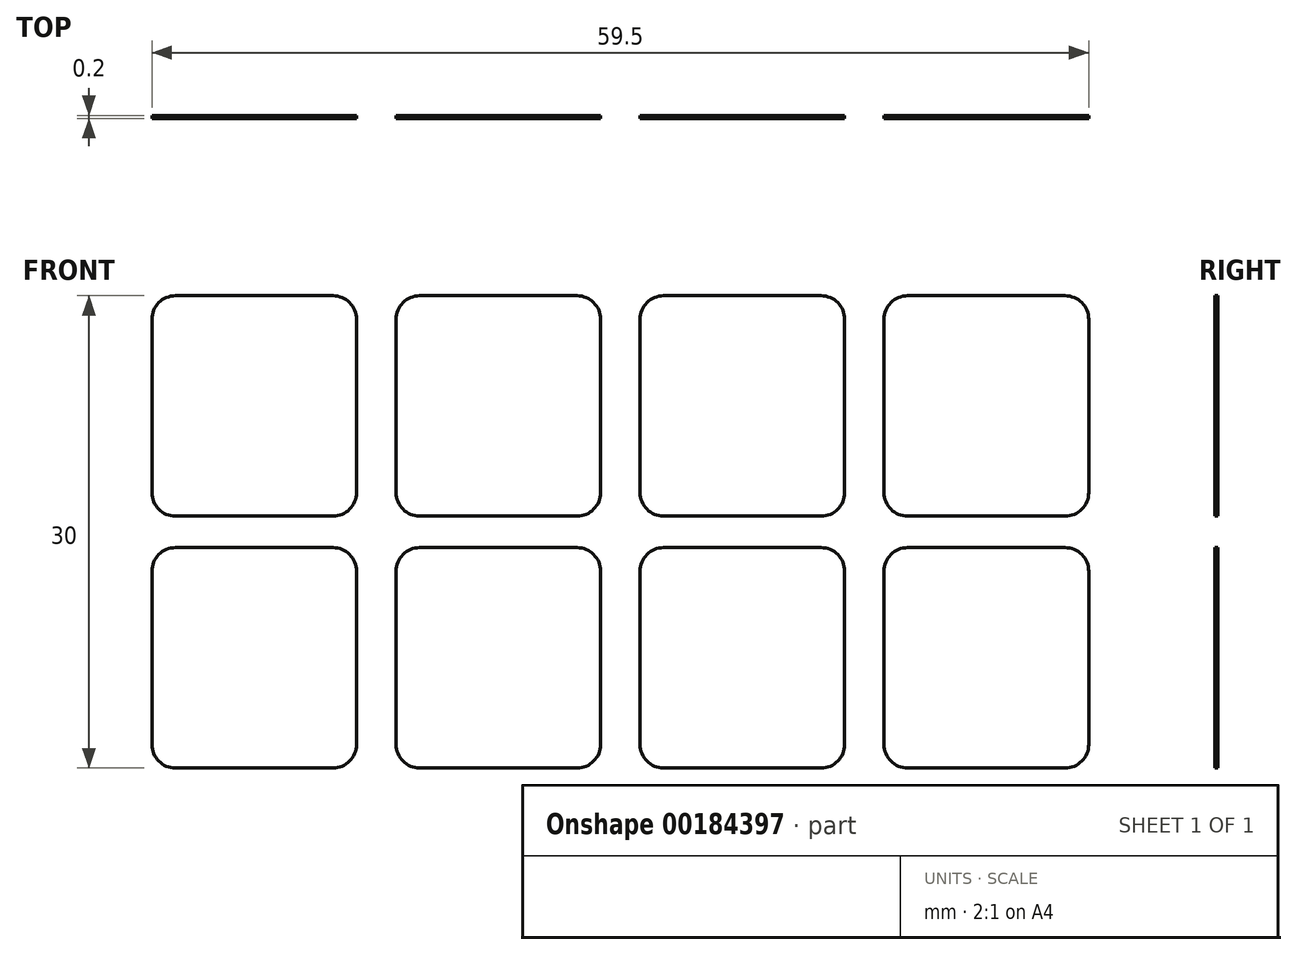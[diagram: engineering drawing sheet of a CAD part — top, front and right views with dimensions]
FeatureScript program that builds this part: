
annotation { "Feature Type Name" : "Feature", "Feature Type Description" : "" }
export const myFeature = defineFeature(function(context is Context, id is Id, definition is map)
    precondition{}
    {
        {
            var Q0;
            Q0=qCreatedBy(makeId("Front.planeOp"),FACE);
            var sketch = newSketch(context, id + "F0", { "sketchPlane" : qUnion([Q0])});
            skLineSegment(sketch, "E0.bottom", {"start": v(1.5, 0) * mm, "end": v(11.5, 0) * mm});
            skLineSegment(sketch, "E0.top", {"start": v(1.5, 14) * mm, "end": v(11.5, 14) * mm});
            skLineSegment(sketch, "E0.left", {"start": v(0, 1.5) * mm, "end": v(0, 12.5) * mm});
            skLineSegment(sketch, "E0.right", {"start": v(13, 1.5) * mm, "end": v(13, 12.5) * mm});
            skPoint(sketch, "E1.visualSharp", {"position": v(0, 14) * mm});
            skArc(sketch, "E1.filletArc", {"start": v(1.5, 14) * mm, "mid": v(0.44, 13.56) * mm, "end": v(0, 12.5) * mm});
            skPoint(sketch, "E2.visualSharp", {"position": v(13, 14) * mm});
            skArc(sketch, "E2.filletArc", {"start": v(13, 12.5) * mm, "mid": v(12.56, 13.56) * mm, "end": v(11.5, 14) * mm});
            skPoint(sketch, "E3.visualSharp", {"position": v(13, 0) * mm});
            skArc(sketch, "E3.filletArc", {"start": v(11.5, 0) * mm, "mid": v(12.56, 0.44) * mm, "end": v(13, 1.5) * mm});
            skPoint(sketch, "E4.visualSharp", {"position": v(0, 0) * mm});
            skArc(sketch, "E4.filletArc", {"start": v(0, 1.5) * mm, "mid": v(0.44, 0.44) * mm, "end": v(1.5, 0) * mm});
            skPoint(sketch, "E5.0.1.0", {"position": v(13, 30) * mm});
            skPoint(sketch, "E5.0.1.1", {"position": v(0, 30) * mm});
            skLineSegment(sketch, "E5.0.1.2", {"start": v(13, 17.5) * mm, "end": v(13, 28.5) * mm});
            skLineSegment(sketch, "E5.0.1.3", {"start": v(0, 17.5) * mm, "end": v(0, 28.5) * mm});
            skPoint(sketch, "E5.0.1.4", {"position": v(13, 16) * mm});
            skLineSegment(sketch, "E5.0.1.5", {"start": v(1.5, 30) * mm, "end": v(11.5, 30) * mm});
            skLineSegment(sketch, "E5.0.1.6", {"start": v(1.5, 16) * mm, "end": v(11.5, 16) * mm});
            skPoint(sketch, "E5.0.1.7", {"position": v(0, 16) * mm});
            skArc(sketch, "E5.0.1.8", {"start": v(0, 17.5) * mm, "mid": v(0.44, 16.44) * mm, "end": v(1.5, 16) * mm});
            skArc(sketch, "E5.0.1.9", {"start": v(1.5, 30) * mm, "mid": v(0.44, 29.56) * mm, "end": v(0, 28.5) * mm});
            skArc(sketch, "E5.0.1.10", {"start": v(13, 28.5) * mm, "mid": v(12.56, 29.56) * mm, "end": v(11.5, 30) * mm});
            skArc(sketch, "E5.0.1.11", {"start": v(11.5, 16) * mm, "mid": v(12.56, 16.44) * mm, "end": v(13, 17.5) * mm});
            skPoint(sketch, "E5.1.0.0", {"position": v(28.5, 14) * mm});
            skPoint(sketch, "E5.1.0.1", {"position": v(15.5, 14) * mm});
            skLineSegment(sketch, "E5.1.0.2", {"start": v(28.5, 1.5) * mm, "end": v(28.5, 12.5) * mm});
            skLineSegment(sketch, "E5.1.0.3", {"start": v(15.5, 1.5) * mm, "end": v(15.5, 12.5) * mm});
            skPoint(sketch, "E5.1.0.4", {"position": v(28.5, 0) * mm});
            skLineSegment(sketch, "E5.1.0.5", {"start": v(17, 14) * mm, "end": v(27, 14) * mm});
            skLineSegment(sketch, "E5.1.0.6", {"start": v(17, 0) * mm, "end": v(27, 0) * mm});
            skPoint(sketch, "E5.1.0.7", {"position": v(15.5, 0) * mm});
            skArc(sketch, "E5.1.0.8", {"start": v(15.5, 1.5) * mm, "mid": v(15.94, 0.44) * mm, "end": v(17, 0) * mm});
            skArc(sketch, "E5.1.0.9", {"start": v(17, 14) * mm, "mid": v(15.94, 13.56) * mm, "end": v(15.5, 12.5) * mm});
            skArc(sketch, "E5.1.0.10", {"start": v(28.5, 12.5) * mm, "mid": v(28.06, 13.56) * mm, "end": v(27, 14) * mm});
            skArc(sketch, "E5.1.0.11", {"start": v(27, 0) * mm, "mid": v(28.06, 0.44) * mm, "end": v(28.5, 1.5) * mm});
            skPoint(sketch, "E5.1.1.0", {"position": v(28.5, 30) * mm});
            skPoint(sketch, "E5.1.1.1", {"position": v(15.5, 30) * mm});
            skLineSegment(sketch, "E5.1.1.2", {"start": v(28.5, 17.5) * mm, "end": v(28.5, 28.5) * mm});
            skLineSegment(sketch, "E5.1.1.3", {"start": v(15.5, 17.5) * mm, "end": v(15.5, 28.5) * mm});
            skPoint(sketch, "E5.1.1.4", {"position": v(28.5, 16) * mm});
            skLineSegment(sketch, "E5.1.1.5", {"start": v(17, 30) * mm, "end": v(27, 30) * mm});
            skLineSegment(sketch, "E5.1.1.6", {"start": v(17, 16) * mm, "end": v(27, 16) * mm});
            skPoint(sketch, "E5.1.1.7", {"position": v(15.5, 16) * mm});
            skArc(sketch, "E5.1.1.8", {"start": v(15.5, 17.5) * mm, "mid": v(15.94, 16.44) * mm, "end": v(17, 16) * mm});
            skArc(sketch, "E5.1.1.9", {"start": v(17, 30) * mm, "mid": v(15.94, 29.56) * mm, "end": v(15.5, 28.5) * mm});
            skArc(sketch, "E5.1.1.10", {"start": v(28.5, 28.5) * mm, "mid": v(28.06, 29.56) * mm, "end": v(27, 30) * mm});
            skArc(sketch, "E5.1.1.11", {"start": v(27, 16) * mm, "mid": v(28.06, 16.44) * mm, "end": v(28.5, 17.5) * mm});
            skPoint(sketch, "E5.2.0.0", {"position": v(44, 14) * mm});
            skPoint(sketch, "E5.2.0.1", {"position": v(31, 14) * mm});
            skLineSegment(sketch, "E5.2.0.2", {"start": v(44, 1.5) * mm, "end": v(44, 12.5) * mm});
            skLineSegment(sketch, "E5.2.0.3", {"start": v(31, 1.5) * mm, "end": v(31, 12.5) * mm});
            skPoint(sketch, "E5.2.0.4", {"position": v(44, 0) * mm});
            skLineSegment(sketch, "E5.2.0.5", {"start": v(32.5, 14) * mm, "end": v(42.5, 14) * mm});
            skLineSegment(sketch, "E5.2.0.6", {"start": v(32.5, 0) * mm, "end": v(42.5, 0) * mm});
            skPoint(sketch, "E5.2.0.7", {"position": v(31, 0) * mm});
            skArc(sketch, "E5.2.0.8", {"start": v(31, 1.5) * mm, "mid": v(31.44, 0.44) * mm, "end": v(32.5, 0) * mm});
            skArc(sketch, "E5.2.0.9", {"start": v(32.5, 14) * mm, "mid": v(31.44, 13.56) * mm, "end": v(31, 12.5) * mm});
            skArc(sketch, "E5.2.0.10", {"start": v(44, 12.5) * mm, "mid": v(43.56, 13.56) * mm, "end": v(42.5, 14) * mm});
            skArc(sketch, "E5.2.0.11", {"start": v(42.5, 0) * mm, "mid": v(43.56, 0.44) * mm, "end": v(44, 1.5) * mm});
            skPoint(sketch, "E5.2.1.0", {"position": v(44, 30) * mm});
            skPoint(sketch, "E5.2.1.1", {"position": v(31, 30) * mm});
            skLineSegment(sketch, "E5.2.1.2", {"start": v(44, 17.5) * mm, "end": v(44, 28.5) * mm});
            skLineSegment(sketch, "E5.2.1.3", {"start": v(31, 17.5) * mm, "end": v(31, 28.5) * mm});
            skPoint(sketch, "E5.2.1.4", {"position": v(44, 16) * mm});
            skLineSegment(sketch, "E5.2.1.5", {"start": v(32.5, 30) * mm, "end": v(42.5, 30) * mm});
            skLineSegment(sketch, "E5.2.1.6", {"start": v(32.5, 16) * mm, "end": v(42.5, 16) * mm});
            skPoint(sketch, "E5.2.1.7", {"position": v(31, 16) * mm});
            skArc(sketch, "E5.2.1.8", {"start": v(31, 17.5) * mm, "mid": v(31.44, 16.44) * mm, "end": v(32.5, 16) * mm});
            skArc(sketch, "E5.2.1.9", {"start": v(32.5, 30) * mm, "mid": v(31.44, 29.56) * mm, "end": v(31, 28.5) * mm});
            skArc(sketch, "E5.2.1.10", {"start": v(44, 28.5) * mm, "mid": v(43.56, 29.56) * mm, "end": v(42.5, 30) * mm});
            skArc(sketch, "E5.2.1.11", {"start": v(42.5, 16) * mm, "mid": v(43.56, 16.44) * mm, "end": v(44, 17.5) * mm});
            skPoint(sketch, "E5.3.0.0", {"position": v(59.5, 14) * mm});
            skPoint(sketch, "E5.3.0.1", {"position": v(46.5, 14) * mm});
            skLineSegment(sketch, "E5.3.0.2", {"start": v(59.5, 1.5) * mm, "end": v(59.5, 12.5) * mm});
            skLineSegment(sketch, "E5.3.0.3", {"start": v(46.5, 1.5) * mm, "end": v(46.5, 12.5) * mm});
            skPoint(sketch, "E5.3.0.4", {"position": v(59.5, 0) * mm});
            skLineSegment(sketch, "E5.3.0.5", {"start": v(48, 14) * mm, "end": v(58, 14) * mm});
            skLineSegment(sketch, "E5.3.0.6", {"start": v(48, 0) * mm, "end": v(58, 0) * mm});
            skPoint(sketch, "E5.3.0.7", {"position": v(46.5, 0) * mm});
            skArc(sketch, "E5.3.0.8", {"start": v(46.5, 1.5) * mm, "mid": v(46.94, 0.44) * mm, "end": v(48, 0) * mm});
            skArc(sketch, "E5.3.0.9", {"start": v(48, 14) * mm, "mid": v(46.94, 13.56) * mm, "end": v(46.5, 12.5) * mm});
            skArc(sketch, "E5.3.0.10", {"start": v(59.5, 12.5) * mm, "mid": v(59.06, 13.56) * mm, "end": v(58, 14) * mm});
            skArc(sketch, "E5.3.0.11", {"start": v(58, 0) * mm, "mid": v(59.06, 0.44) * mm, "end": v(59.5, 1.5) * mm});
            skPoint(sketch, "E5.3.1.0", {"position": v(59.5, 30) * mm});
            skPoint(sketch, "E5.3.1.1", {"position": v(46.5, 30) * mm});
            skLineSegment(sketch, "E5.3.1.2", {"start": v(59.5, 17.5) * mm, "end": v(59.5, 28.5) * mm});
            skLineSegment(sketch, "E5.3.1.3", {"start": v(46.5, 17.5) * mm, "end": v(46.5, 28.5) * mm});
            skPoint(sketch, "E5.3.1.4", {"position": v(59.5, 16) * mm});
            skLineSegment(sketch, "E5.3.1.5", {"start": v(48, 30) * mm, "end": v(58, 30) * mm});
            skLineSegment(sketch, "E5.3.1.6", {"start": v(48, 16) * mm, "end": v(58, 16) * mm});
            skPoint(sketch, "E5.3.1.7", {"position": v(46.5, 16) * mm});
            skArc(sketch, "E5.3.1.8", {"start": v(46.5, 17.5) * mm, "mid": v(46.94, 16.44) * mm, "end": v(48, 16) * mm});
            skArc(sketch, "E5.3.1.9", {"start": v(48, 30) * mm, "mid": v(46.94, 29.56) * mm, "end": v(46.5, 28.5) * mm});
            skArc(sketch, "E5.3.1.10", {"start": v(59.5, 28.5) * mm, "mid": v(59.06, 29.56) * mm, "end": v(58, 30) * mm});
            skArc(sketch, "E5.3.1.11", {"start": v(58, 16) * mm, "mid": v(59.06, 16.44) * mm, "end": v(59.5, 17.5) * mm});
            skLineSegment(sketch, "E5.direction1", {"start": v(0, 0) * mm, "end": v(15.5, 0) * mm, "construction": true});
            skLineSegment(sketch, "E5.direction2", {"start": v(0, 0) * mm, "end": v(0, 16) * mm, "construction": true});
            skSolve(sketch);
        }
        {
            var Q0;
            Q0 = qSketchRegion(id + "F0", true);
            extrude(context, id + "F1", {"entities" : qUnion([Q0]), "depth" : 0.2 * mm});
        }
    });
